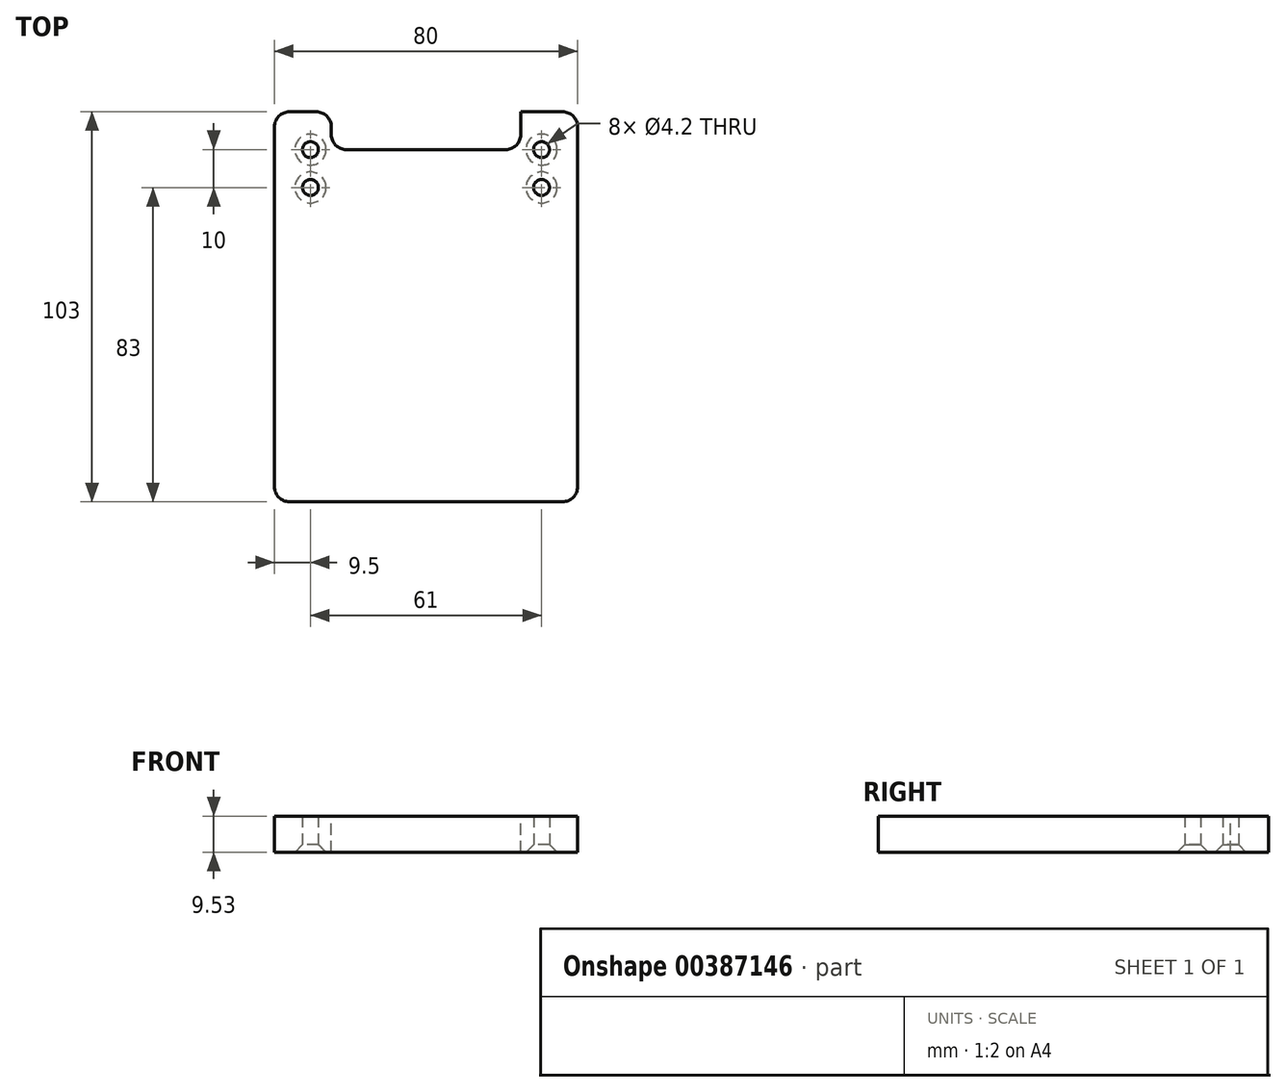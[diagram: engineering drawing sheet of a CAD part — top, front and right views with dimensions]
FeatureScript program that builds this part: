
annotation { "Feature Type Name" : "Feature", "Feature Type Description" : "" }
export const myFeature = defineFeature(function(context is Context, id is Id, definition is map)
    precondition{}
    {
        {
            var Q0;
            Q0=qCreatedBy(makeId("Top.planeOp"),FACE);
            var sketch = newSketch(context, id + "F0", { "sketchPlane" : qUnion([Q0])});
            skLineSegment(sketch, "E0.bottom", {"start": v(36, 51.5) * mm, "end": v(-36, 51.5) * mm});
            skLineSegment(sketch, "E0.top", {"start": v(36, -51.5) * mm, "end": v(-36, -51.5) * mm});
            skLineSegment(sketch, "E0.left", {"start": v(40, 47.5) * mm, "end": v(40, -47.5) * mm});
            skLineSegment(sketch, "E0.right", {"start": v(-40, 47.5) * mm, "end": v(-40, -47.5) * mm});
            skPoint(sketch, "E0.middle", {"position": v(0, 0) * mm});
            skPoint(sketch, "E1.visualSharp", {"position": v(-40, 51.5) * mm});
            skArc(sketch, "E1.filletArc", {"start": v(-36, 51.5) * mm, "mid": v(-38.83, 50.33) * mm, "end": v(-40, 47.5) * mm});
            skPoint(sketch, "E2.visualSharp", {"position": v(40, 51.5) * mm});
            skArc(sketch, "E2.filletArc", {"start": v(40, 47.5) * mm, "mid": v(38.83, 50.33) * mm, "end": v(36, 51.5) * mm});
            skPoint(sketch, "E3.visualSharp", {"position": v(-40, -51.5) * mm});
            skArc(sketch, "E3.filletArc", {"start": v(-40, -47.5) * mm, "mid": v(-38.83, -50.33) * mm, "end": v(-36, -51.5) * mm});
            skPoint(sketch, "E4.visualSharp", {"position": v(40, -51.5) * mm});
            skArc(sketch, "E4.filletArc", {"start": v(36, -51.5) * mm, "mid": v(38.83, -50.33) * mm, "end": v(40, -47.5) * mm});
            skCircle(sketch, "E5", {"center": v(-30.5, 41.5) * mm, "radius": 2.1 * mm});
            skCircle(sketch, "E6", {"center": v(-30.5, 31.5) * mm, "radius": 2.1 * mm});
            skCircle(sketch, "E7", {"center": v(30.5, 41.5) * mm, "radius": 2.1 * mm});
            skCircle(sketch, "E8", {"center": v(30.5, 31.5) * mm, "radius": 2.1 * mm});
            skSolve(sketch);
        }
        {
            var Q0;
            Q0 = qSketchRegion(id + "F0", true);
            extrude(context, id + "F1", {"entities" : qUnion([Q0]), "depth" : 9.53 * mm});
        }
        {
            var Q0;
            Q0=makeQuery(id+"F1.opExtrude","CAP_EDGE",EDGE,{"disambiguationData":[OSD([sQuery(id+"F0.wireOp",EDGE,"E7")])],"isStart":true});
            var Q1;
            Q1=makeQuery(id+"F1.opExtrude","CAP_EDGE",EDGE,{"disambiguationData":[OSD([sQuery(id+"F0.wireOp",EDGE,"E8")])],"isStart":true});
            var Q2;
            Q2=makeQuery(id+"F1.opExtrude","CAP_EDGE",EDGE,{"disambiguationData":[OSD([sQuery(id+"F0.wireOp",EDGE,"E6")])],"isStart":true});
            var Q3;
            Q3=makeQuery(id+"F1.opExtrude","CAP_EDGE",EDGE,{"disambiguationData":[OSD([sQuery(id+"F0.wireOp",EDGE,"E5")])],"isStart":true});
            chamfer(context, id + "F2", {"entities" : qUnion([Q0, Q1, Q2, Q3]), "chamferType" : ChamferType.OFFSET_ANGLE, "width" : 2 * mm, "oppositeDirection" : false, "angle" : 45 * degree, "tangentPropagation" : true});
        }
        {
            var Q0;
            Q0=makeQuery(id+"F1.opExtrude","CAP_FACE",FACE,{"disambiguationData":[OSD([sQuery(id+"F0.wireOp",EDGE,"E0.bottom"),sQuery(id+"F0.wireOp",EDGE,"E0.top"),sQuery(id+"F0.wireOp",EDGE,"E0.left"),sQuery(id+"F0.wireOp",EDGE,"E0.right"),sQuery(id+"F0.wireOp",EDGE,"E1.filletArc"),sQuery(id+"F0.wireOp",EDGE,"E2.filletArc"),sQuery(id+"F0.wireOp",EDGE,"E3.filletArc"),sQuery(id+"F0.wireOp",EDGE,"E4.filletArc"),sQuery(id+"F0.wireOp",EDGE,"E5"),sQuery(id+"F0.wireOp",EDGE,"E6"),sQuery(id+"F0.wireOp",EDGE,"E7"),sQuery(id+"F0.wireOp",EDGE,"E8")])],"isStart":false});
            var sketch = newSketch(context, id + "F3", { "sketchPlane" : qUnion([Q0])});
            skPoint(sketch, "E9.endSnap0", {"position": v(0, 51.5) * mm});
            skLineSegment(sketch, "E10", {"start": v(-25, 41.5) * mm, "end": v(25, 41.5) * mm});
            skLineSegment(sketch, "E11", {"start": v(-25, 41.5) * mm, "end": v(-25, 51.5) * mm});
            skLineSegment(sketch, "E12", {"start": v(-25, 51.5) * mm, "end": v(25, 51.5) * mm});
            skLineSegment(sketch, "E13", {"start": v(25, 51.5) * mm, "end": v(25, 41.5) * mm});
            skSolve(sketch);
        }
        {
            var Q0;
            Q0 = qSketchRegion(id + "F3", true);
            extrude(context, id + "F4", {"entities" : qUnion([Q0]), "operationType" : NewBodyOperationType.REMOVE, "oppositeDirection" : true, "depth" : 25 * mm});
        }
        {
            var Q0;
            Q0=makeQuery(id+"F4.boolean.opBoolean","COPY",EDGE,{"derivedFrom":makeQuery(id+"F4.opExtrude","SWEPT_EDGE",EDGE,{"disambiguationData":[OSD([sQuery(id+"F0.wireOp",EDGE,"E0.bottom"),sQuery(id+"F3.wireOp",EDGE,"E11"),sQuery(id+"F3.wireOp",EDGE,"E12")])]})});
            var Q1;
            Q1=makeQuery(id+"F4.boolean.opBoolean","COPY",EDGE,{"derivedFrom":makeQuery(id+"F4.opExtrude","SWEPT_EDGE",EDGE,{"disambiguationData":[OSD([sQuery(id+"F0.wireOp",EDGE,"E0.bottom"),sQuery(id+"F3.wireOp",EDGE,"E12"),sQuery(id+"F3.wireOp",EDGE,"E13")])]})});
            fillet(context, id + "F5", {"entities" : qUnion([Q0, Q1]), "radius" : 4 * mm, "tangentPropagation" : true, "allowEdgeOverflow" : false});
        }
        {
            var Q0;
            Q0=makeQuery(id+"F4.boolean.opBoolean","COPY",EDGE,{"derivedFrom":makeQuery(id+"F4.opExtrude","SWEPT_EDGE",EDGE,{"disambiguationData":[OSD([sQuery(id+"F3.wireOp",EDGE,"E10"),sQuery(id+"F3.wireOp",EDGE,"E13")])]})});
            var Q1;
            Q1=makeQuery(id+"F4.boolean.opBoolean","COPY",EDGE,{"derivedFrom":makeQuery(id+"F4.opExtrude","SWEPT_EDGE",EDGE,{"disambiguationData":[OSD([sQuery(id+"F3.wireOp",EDGE,"E10"),sQuery(id+"F3.wireOp",EDGE,"E11")])]})});
            fillet(context, id + "F6", {"entities" : qUnion([Q0, Q1]), "radius" : 4 * mm, "tangentPropagation" : true, "allowEdgeOverflow" : false});
        }
    });
